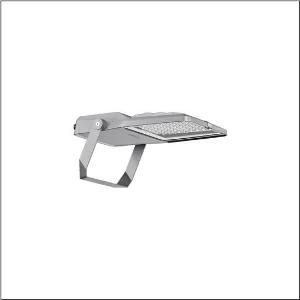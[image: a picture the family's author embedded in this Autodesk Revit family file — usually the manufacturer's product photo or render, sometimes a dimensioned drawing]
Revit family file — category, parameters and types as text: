
# Revit family: floodlight_fl_21_iq_mini___pl61_5xa7771c4c1a_e46d
name_source: partatom
category: Lighting Fixtures
units: mm (PartAtom-declared; Revit-internal decimal feet)

## family parameters
Cut with Voids When Loaded = No
Host = Face
Light Source = No
Part Type = Normal
Room Calculation Point = No
Round Connector Dimension = Use Diameter
Shared = No

## types (1)
- --- (1 x LED, 12490 lm, 87.2 W, 4000K)
    Apparent Load = 87 VA
    CIE Flux Codes = 33 65 98 100 100
    Color Rendering = 70
    Color Temperature = 4000K
    Default Elevation = 1800 mm
    Description = Floodlight FL 21 iQ mini, floodlight, primary light control with lens, of PMMA, primary optical cover: protective disc, of toughened safety glass, transparent, light distribution: PL61, light emission: direct distribution, installation type: surface-mounted, lamps: LED, High Power LED, rated values: 12.490lm | 87,2W | 143,2lm/W (begin service life); end service life: 12.490lm | 92,1W; at 50% lumin. flux: 6.245lm | 40,2W | 155,3lm/W, colour temperature: 4000K, colour rendering: CRI > 70, light colour: 740, light setting 1 begin service life: 100% | 12.490lm | 87,2W | 143,2lm/W | 4.000K, light setting 1 end service life: 92,1W, further light settings possible, control: Auto-Match, Temp-Guard, Lumen-Switch, Night-Set, Smart-Wire, Light-Fading, Desk-Remote (wireless, voltage-free reading and setting of iQ features in the workshop via application-optimized NFC function/RFID function), optimised constant luminous flux control (CLO 2.0), pre-setting: linear dimming characteristic, with terminal, 6-pole, mains connection: 220..240V, AC, 50/60Hz, luminaire housing, of diecast aluminium, powder-coated, SITECO metallic grey (DB 702S), corrosivity category C5 mid according to DIN EN ISO 12944suitable for swimming poolschlorine-resistant, sealing non-destructively replaceable, mounting bracket, of steel, galvanised, powder-coated, SITECO metallic grey (DB 702S), protection rating (complete): IP66, insulation class (complete): insulation class II (safety insulation), certification: CE, ENEC, VDE, protection symbol: D, impact resistance: IK08, permissible operating ambient temperature: -40..+40°C, permissible operating ambient temperature for outdoor applications: -40..+50°C, standard: DIN EN 12944, LABS conformity tested according to VDMA 24364:2018-05, packaging unit: 1 piece

Light Distribution: PL61
    Height = 70 mm
    Lamp = 1 x LED
    Lamp Light Flux = 12490 lm
    Lamp Power = 87.2 W
    Lamp count = 1
    Length = 485 mm
    Luminous efficacy = 143 lm/W
    Manufacturer = Siteco
    ModVariant = No
    Model = 5XA7771C4C1A
    Mounting Place = Pole
    Mounting Type = Pole annexe
    Number of Poles = 1
    OnlyDefault = Yes
    Power Factor = 1
    Product Name = Floodlight FL 21 iQ mini | PL61
    Product group = floodlight | pylon annexe
    ProductGroupID = 6201
    Protection Class = Protection class II
    Protection Degree = IP 66
    RLX_Detail_Level = 1
    RLX_Emergency_Light_Flux = 0 lm
    RLX_Emergency_Type = 0
    RLX_Emergency_Type_DB = No
    RlxData = <blob elided: 96521 chars, md5=ccff49bc>
    Socket = socket
    Standby Power = 0 W
    System Light Flux = 12490 lm
    System Power = 87 W
    Type Comments = factory setting: luminous flux: 100 % | dim-lin: 254 | 456 mA
    Type Image = l_1006845.jpg
    URL = http://relux.com
    VarID = @adj_174301
    Voltage = 0 V
    Weight = 0.00 kg
    Width = 337 mm

## geometry (parser evidence)
native form markers: Blend x4, Sweep x13
no freeform markers — native parametric forms only
